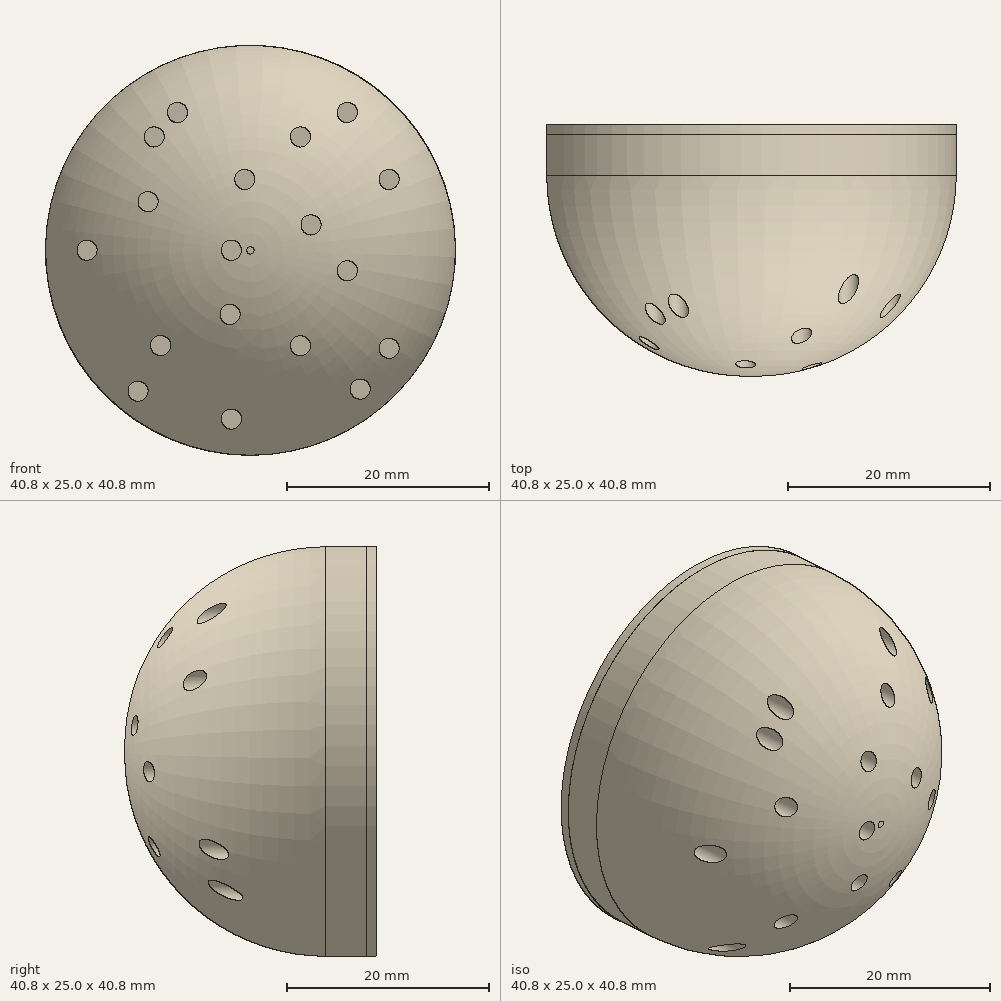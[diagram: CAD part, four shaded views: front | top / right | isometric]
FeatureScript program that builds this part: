
annotation { "Feature Type Name" : "Feature", "Feature Type Description" : "" }
export const myFeature = defineFeature(function(context is Context, id is Id, definition is map)
    precondition{}
    {
        {
            var Q0;
            Q0=qCreatedBy(makeId("Front.planeOp"),FACE);
            var sketch = newSketch(context, id + "F0", { "sketchPlane" : qUnion([Q0])});
            skCircle(sketch, "E0", {"center": v(0, 0) * mm, "radius": 20.37 * mm});
            skCircle(sketch, "E1", {"center": v(-1.9, -16.78) * mm, "radius": 1 * mm});
            skCircle(sketch, "E2", {"center": v(-1.9, 0) * mm, "radius": 1 * mm});
            skCircle(sketch, "E3", {"center": v(-16.24, 0) * mm, "radius": 1 * mm});
            skCircle(sketch, "E4", {"center": v(9.64, -2.04) * mm, "radius": 1 * mm});
            skCircle(sketch, "E5", {"center": v(9.64, 13.7) * mm, "radius": 1 * mm});
            skCircle(sketch, "E6", {"center": v(-7.25, 13.7) * mm, "radius": 1 * mm});
            skCircle(sketch, "E7", {"center": v(4.98, -9.5) * mm, "radius": 1 * mm});
            skCircle(sketch, "E8", {"center": v(4.98, 11.27) * mm, "radius": 1 * mm});
            skCircle(sketch, "E9", {"center": v(-9.57, 11.27) * mm, "radius": 1 * mm});
            skCircle(sketch, "E10", {"center": v(13.79, -9.74) * mm, "radius": 1 * mm});
            skCircle(sketch, "E11", {"center": v(13.79, 7.04) * mm, "radius": 1 * mm});
            skCircle(sketch, "E12", {"center": v(-0.56, 7.04) * mm, "radius": 1 * mm});
            skCircle(sketch, "E13", {"center": v(6.02, 2.52) * mm, "radius": 1 * mm});
            skCircle(sketch, "E14", {"center": v(-10.18, 4.83) * mm, "radius": 1 * mm});
            skCircle(sketch, "E15", {"center": v(-8.93, -9.47) * mm, "radius": 1 * mm});
            skCircle(sketch, "E16", {"center": v(10.9, -13.8) * mm, "radius": 1 * mm});
            skCircle(sketch, "E17", {"center": v(-2.03, -6.38) * mm, "radius": 1 * mm});
            skCircle(sketch, "E18", {"center": v(-11.18, -14) * mm, "radius": 1 * mm});
            skSolve(sketch);
        }
        {
            var Q0;
            Q0 = qSketchRegion(id + "F0", true);
            var Q1;
            Q1=makeQuery(id+"F0.imprint","IMPRINT",FACE,{"disambiguationData":[TD([[makeQuery(id+"F0.imprint","IMPRINT",EDGE,{"derivedFrom":sQuery(id+"F0.wireOp",EDGE,"E0")}),1.0]])]});
            extrude(context, id + "F1", {"entities" : qUnion([Q0, Q1]), "depth" : 25 * mm, "offsetDistance" : 25.4 * mm});
        }
        {
            var Q0;
            Q0=makeQuery(id+"F1.opExtrude","CAP_EDGE",EDGE,{"disambiguationData":[OSD([sQuery(id+"F0.wireOp",EDGE,"E0")])],"isStart":false});
            fillet(context, id + "F2", {"entities" : qUnion([Q0]), "radius" : 20 * mm, "tangentPropagation" : true, "allowEdgeOverflow" : false});
        }
        {
            var Q0;
            Q0=qCreatedBy(makeId("Front.planeOp"),FACE);
            var sketch = newSketch(context, id + "F3", { "sketchPlane" : qUnion([Q0])});
            skCircle(sketch, "E19", {"center": v(0, 0) * mm, "radius": 20.38 * mm});
            skSolve(sketch);
        }
        {
            var Q0;
            Q0 = qSketchRegion(id + "F3", true);
            extrude(context, id + "F4", {"entities" : qUnion([Q0]), "operationType" : NewBodyOperationType.ADD, "depth" : 1 * mm, "offsetDistance" : 25 * mm});
        }
    });
